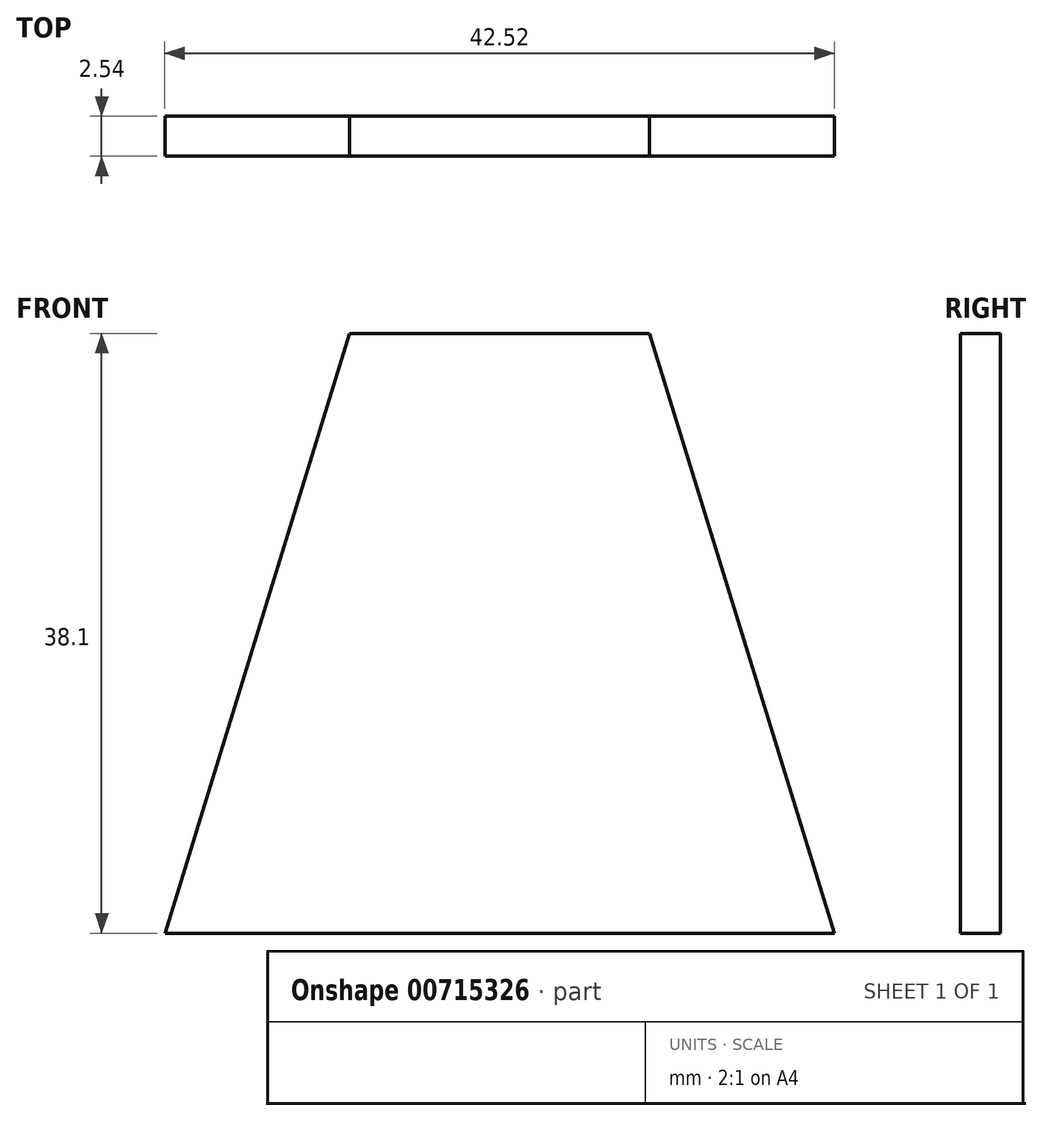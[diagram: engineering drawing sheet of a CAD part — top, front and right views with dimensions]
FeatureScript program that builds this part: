
annotation { "Feature Type Name" : "Feature", "Feature Type Description" : "" }
export const myFeature = defineFeature(function(context is Context, id is Id, definition is map)
    precondition{}
    {
        {
            var Q0;
            Q0=qCreatedBy(makeId("Front.planeOp"),FACE);
            var sketch = newSketch(context, id + "F0", { "sketchPlane" : qUnion([Q0])});
            skLineSegment(sketch, "E0", {"start": v(0, 0) * mm, "end": v(0, 38.1) * mm});
            skLineSegment(sketch, "E1", {"start": v(0, 38.1) * mm, "end": v(-9.53, 38.1) * mm});
            skLineSegment(sketch, "E2", {"start": v(-9.53, 38.1) * mm, "end": v(-21.26, 0) * mm});
            skLineSegment(sketch, "E3", {"start": v(0, 38.1) * mm, "end": v(9.52, 38.1) * mm});
            skLineSegment(sketch, "E4", {"start": v(-21.26, 0) * mm, "end": v(0, 0) * mm});
            skLineSegment(sketch, "E5", {"start": v(0, 0) * mm, "end": v(21.26, 0) * mm});
            skLineSegment(sketch, "E6", {"start": v(21.26, 0) * mm, "end": v(9.52, 38.1) * mm});
            skSolve(sketch);
        }
        {
            var Q0;
            Q0 = qSketchRegion(id + "F0", true);
            extrude(context, id + "F1", {"entities" : qUnion([Q0]), "depth" : 2.54 * mm, "offsetDistance" : 25.4 * mm});
        }
    });
